# Revit family: Gira_291403
name_source: partatom
category: Electrical Fixtures
revit_build: Autodesk Revit 2017 (Build: 20160225_1515(x64)
units: mm (PartAtom-declared; Revit-internal decimal feet)

## family parameters
Cut with Voids When Loaded = No
Host = Face
Maintain Annotation Orientation = Yes
Part Type = Normal
Room Calculation Point = No
Round Connector Dimension = Use Diameter
Shared = No

## types (1)
- Emergency set System 55 p.white
    Available = No
    BIM (1) = https://media.stage.bim.site und Tasten.rfa?public/gira/36a6b08/Sys55_Komplettgerät_Schalten und Tasten.rfa
    Button function = Activate/quit call
    Category = Call-/control unit clinic-installation
    Construction = Wall model
    Data sheet (1) = https://katalog.gira.de
    Default Elevation = 1219 mm
    Description = Emerg.set Sys55 PW,Emergency set,System 55,pure white glossy,Features:,- Call module with red LED signal light, integrated zero-voltage contact, optionally activated buzzer (continuous tone) and the option of setting either flashing light or continuous light.,- Pull-cord button with 2.5 m pull cord with red handle and reassurance light in button housing, suitable for wall or ceiling mounting.,- Switch-off button with integrated green button.,- Flush-mounted power supply unit 250 mA.,- As an option, the call set can be expanded with a duty room unit with an integrated sound generator for acoustic call signalling, a green presence button with presence light, and a yellow buzzer switch-off button.,,Notes :,- Use uninterruptible power supply for installation pursuant to DIN 0834.,- Individual components can be purchased later to extend the emergency sets.
    GTIN = 4010337067900
    HAN = 291403
    HeinzeBIM = https://bimportal.heinze.de
    Manufacturer = Gira
    Manufacturer URL = https://www.gira.de
    Model = Sys55_Komplettgerät_Schalten und Tasten
    Name = Emergency set System 55 p.white
    Suitable for = Emergency call
    Suitable for bus connection = 2-wire
    URL = http://katalog.gira.de

## geometry (parser evidence)
native form markers: Blend x2, Sweep x6
no freeform markers — native parametric forms only
